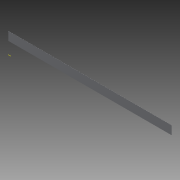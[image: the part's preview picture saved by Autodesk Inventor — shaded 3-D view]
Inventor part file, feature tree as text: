
AUTODESK INVENTOR PART (.ipt)
format: ipt  version: 2013 (Build 170138000, 138)  size: 102,400 bytes
history: native  units: in
note: dims shown in document units (in); Inventor stores cm internally (conversion verified against a paired STEP export)
features: extrude x4, sketch x4, plane x1
ambient origin geometry x8: Origin, YZ Plane, XZ Plane, XY Plane, X Axis, Y Axis, Z Axis, Center Point
bodies: Solid1 (feature_tree)
feature tree (9):
  plane  "Work Plane1"
  extrude  "Extrusion1"  Depth=1.0in
  extrude  "Extrusion2"  Depth=18.99in
  extrude  "Extrusion3"  Depth=0.01in TaperAngle=0.0deg
  extrude  "Extrusion4"  Depth=0.01in TaperAngle=0.0deg
  sketch  "Sketch1"  dims[d0=18.99in d1=1.0in]
  sketch  "Sketch2"  dims[d2=0.25in d3=18.99in]
  sketch  "Sketch3"  dims[d4=1.0in d5=0.01in d6=0.0in]
  sketch  "Sketch4"  dims[d7=0.01in d8=0.0in d9=0.01in d10=0.0in d11=0.01in d12=1.0in d13=0.01in d14=1.0in d15=1.0in d16=0.0in]
